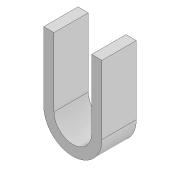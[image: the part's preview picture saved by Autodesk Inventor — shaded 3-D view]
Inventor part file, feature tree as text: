
AUTODESK INVENTOR PART (.ipt)
format: ipt  version: 2022 (Build 260153000, 153)  size: 90,624 bytes
history: native  units: mm
features: extrude x1, sketch x1
ambient origin geometry x8: Origin, YZ Plane, XZ Plane, XY Plane, X Axis, Y Axis, Z Axis, Center Point
bodies: Solid1 (feature_tree)
feature tree (2):
  extrude  "Extrusion1"  Depth=3.0mm
  sketch  "Sketch1"  dims[d0=3.0mm d1=3.0mm d2=5.5mm d3=5.5mm d4=20.0mm d5=20.0mm d6=10.0mm d7=0.0mm]
